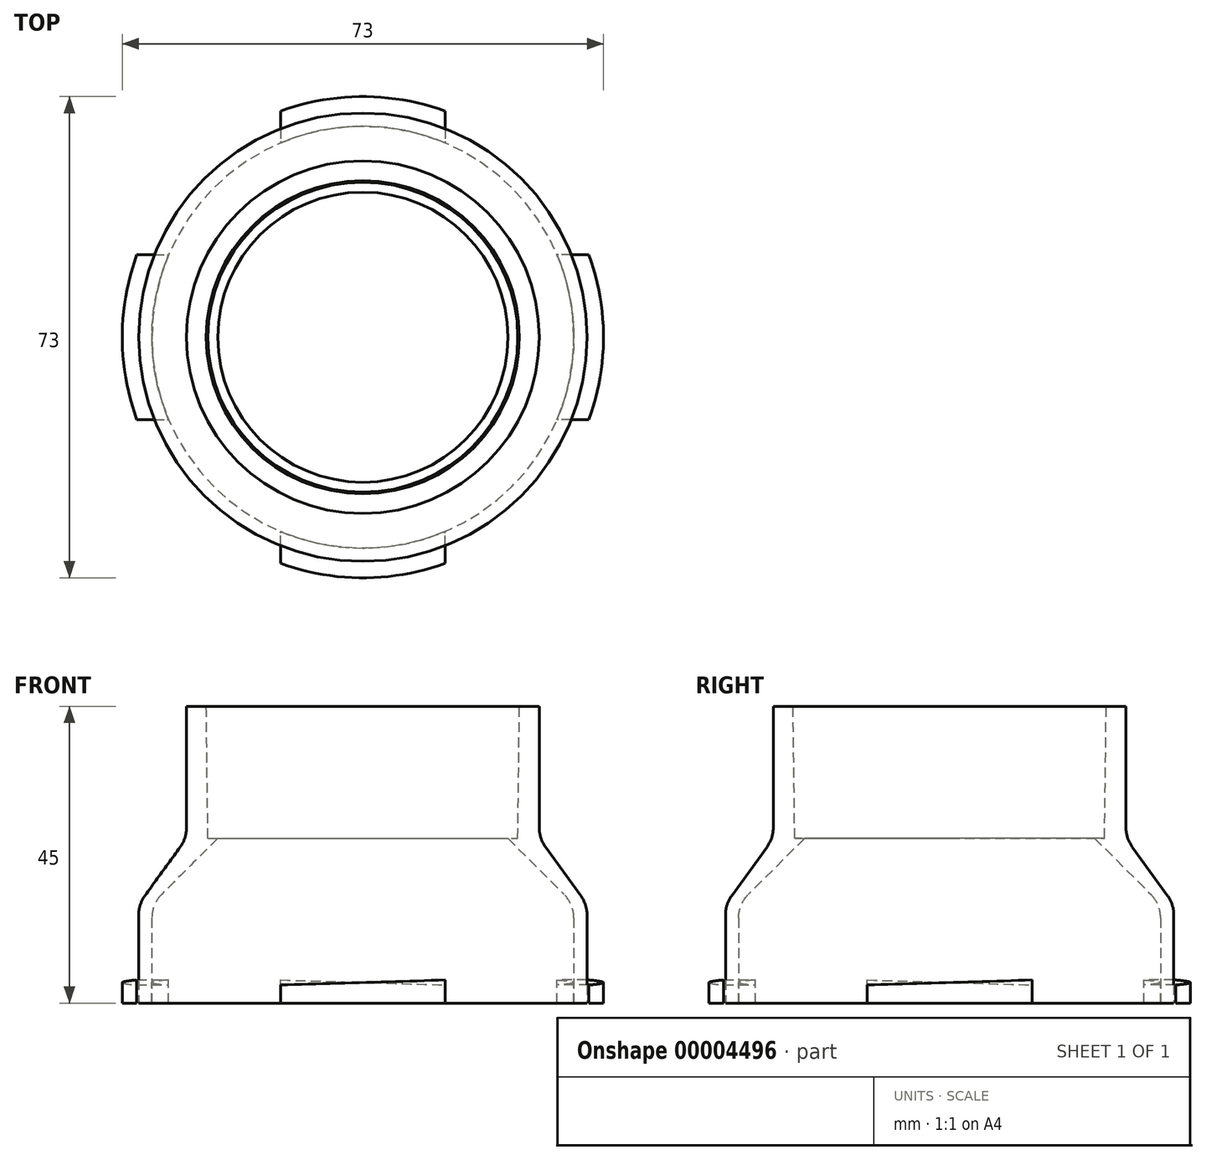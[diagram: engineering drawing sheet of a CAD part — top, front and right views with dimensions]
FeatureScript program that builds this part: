
annotation { "Feature Type Name" : "Feature", "Feature Type Description" : "" }
export const myFeature = defineFeature(function(context is Context, id is Id, definition is map)
    precondition{}
    {
        {
            var Q0;
            Q0=qCreatedBy(makeId("Front.planeOp"),FACE);
            var sketch = newSketch(context, id + "F0", { "sketchPlane" : qUnion([Q0])});
            skLineSegment(sketch, "E0", {"start": v(0, 0) * mm, "end": v(0, 61.44) * mm, "construction": true});
            skLineSegment(sketch, "E1", {"start": v(-32, 15) * mm, "end": v(-32, 0) * mm});
            skLineSegment(sketch, "E2", {"start": v(-32, 0) * mm, "end": v(-34, 0) * mm});
            skLineSegment(sketch, "E3", {"start": v(-34, 0) * mm, "end": v(-34, 15) * mm});
            skLineSegment(sketch, "E4.bottom", {"start": v(-26.75, 45) * mm, "end": v(-23.75, 45) * mm});
            skLineSegment(sketch, "E4.left", {"start": v(-26.75, 45) * mm, "end": v(-26.75, 25) * mm});
            skLineSegment(sketch, "E5", {"start": v(-26.75, 25) * mm, "end": v(-34, 15) * mm});
            skLineSegment(sketch, "E6", {"start": v(-32, 15) * mm, "end": v(-22, 25) * mm});
            skLineSegment(sketch, "E7", {"start": v(-23.75, 45) * mm, "end": v(-23.5, 25) * mm});
            skLineSegment(sketch, "E8", {"start": v(-23.5, 25) * mm, "end": v(-22, 25) * mm});
            skSolve(sketch);
        }
        {
            var Q0;
            Q0=makeQuery(id+"F0.imprint","IMPRINT",FACE,{"disambiguationData":[TD([[makeQuery(id+"F0.imprint","IMPRINT",EDGE,{"derivedFrom":sQuery(id+"F0.wireOp",EDGE,"E1")}),-1.0]])]});
            var Q1;
            Q1=sQuery(id+"F0.wireOp",EDGE,"E0");
            revolve(context, id + "F1", {"entities" : qUnion([Q0]), "axis" : qUnion([Q1]), "revolveType" : RevolveType.FULL});
        }
        {
            var Q0;
            Q0=qCreatedBy(makeId("Front.planeOp"),FACE);
            var sketch = newSketch(context, id + "F2", { "sketchPlane" : qUnion([Q0])});
            skLineSegment(sketch, "E9.top", {"start": v(12.5, 0) * mm, "end": v(0, 0) * mm});
            skLineSegment(sketch, "E9.left", {"start": v(12.5, 2.75) * mm, "end": v(12.5, 0) * mm});
            skLineSegment(sketch, "E10", {"start": v(0, -1.37) * mm, "end": v(0, 27.04) * mm, "construction": true});
            skLineSegment(sketch, "E11", {"start": v(0, 0) * mm, "end": v(-12.5, 0) * mm});
            skLineSegment(sketch, "E12", {"start": v(-12.5, 0) * mm, "end": v(-12.5, 3.5) * mm});
            skLineSegment(sketch, "E13", {"start": v(-12.5, 3.5) * mm, "end": v(12.5, 2.75) * mm});
            skSolve(sketch);
        }
        {
            var Q0;
            Q0=qSketchRegion(id+"F2",true);
            extrude(context, id + "F3", {"entities" : qUnion([Q0]), "oppositeDirection" : true, "depth" : (73 / 2) * mm});
        }
        {
            var Q0;
            Q0=qCreatedBy(makeId("Right.planeOp"),FACE);
            var sketch = newSketch(context, id + "F4", { "sketchPlane" : qUnion([Q0])});
            skLineSegment(sketch, "E14.0", {"start": v(36.5, 0) * mm, "end": v(36.5, 3.5) * mm});
            skLineSegment(sketch, "E15.0", {"start": v(34, 15) * mm, "end": v(-34, 15) * mm, "construction": true});
            skLineSegment(sketch, "E16", {"start": v(0, 0) * mm, "end": v(0, 34.86) * mm, "construction": true});
            skLineSegment(sketch, "E17.bottom", {"start": v(36.5, 3.5) * mm, "end": v(46.5, 3.5) * mm});
            skLineSegment(sketch, "E17.top", {"start": v(36.5, 0) * mm, "end": v(46.5, 0) * mm});
            skLineSegment(sketch, "E17.left", {"start": v(36.5, 3.5) * mm, "end": v(36.5, 0) * mm});
            skLineSegment(sketch, "E17.right", {"start": v(46.5, 3.5) * mm, "end": v(46.5, 0) * mm});
            skLineSegment(sketch, "E18.bottom", {"start": v(36.5, 0) * mm, "end": v(36.5, 0) * mm});
            skLineSegment(sketch, "E18.top", {"start": v(36.5, 0) * mm, "end": v(36.5, 0) * mm});
            skLineSegment(sketch, "E18.left", {"start": v(36.5, 0) * mm, "end": v(36.5, 0) * mm});
            skLineSegment(sketch, "E18.right", {"start": v(36.5, 0) * mm, "end": v(36.5, 0) * mm});
            skLineSegment(sketch, "E19.0", {"start": v(32, 0) * mm, "end": v(-32, 0) * mm, "construction": true});
            skLineSegment(sketch, "E20.bottom", {"start": v(32, 0) * mm, "end": v(0, 0) * mm});
            skLineSegment(sketch, "E20.top", {"start": v(32, 3.5) * mm, "end": v(0, 3.5) * mm});
            skLineSegment(sketch, "E20.left", {"start": v(32, 0) * mm, "end": v(32, 3.5) * mm});
            skLineSegment(sketch, "E20.right", {"start": v(0, 0) * mm, "end": v(0, 3.5) * mm});
            skSolve(sketch);
        }
        {
            var Q0;
            {Q0=qUnion([makeQuery(id+"F4.imprint","IMPRINT",FACE,{"disambiguationData":[TD([[makeQuery(id+"F4.imprint","IMPRINT",EDGE,{"derivedFrom":sQuery(id+"F4.wireOp",EDGE,"E17.bottom")}),-1.0]])]}),makeQuery(id+"F4.imprint","IMPRINT",FACE,{"disambiguationData":[TD([[makeQuery(id+"F4.imprint","IMPRINT",EDGE,{"derivedFrom":sQuery(id+"F4.wireOp",EDGE,"E20.bottom")}),-1.0]])]})]);}
            var Q1;
            Q1=sQuery(id+"F4.wireOp",EDGE,"E16");
            revolve(context, id + "F5", {"operationType" : NewBodyOperationType.REMOVE, "entities" : qUnion([Q0]), "axis" : qUnion([Q1]), "revolveType" : RevolveType.FULL, "oppositeDirection" : true});
        }
        {
            var Q0;
            Q0=makeQuery(id+"F3.opExtrude","SWEPT_BODY",BODY,{"disambiguationData":[OSD([sQuery(id+"F2.wireOp",EDGE,"E9.top"),sQuery(id+"F2.wireOp",EDGE,"E9.left"),sQuery(id+"F2.wireOp",EDGE,"E12"),sQuery(id+"F2.wireOp",EDGE,"E13")])]});
            var Q1;
            Q1=sQuery(id+"F4.wireOp",EDGE,"E16");
            circularPattern(context, id + "F6", {"entities" : qUnion([Q0]), "axis" : qUnion([Q1]), "angle" : 360 * degree, "instanceCount" : round(4), "equalSpace" : true});
        }
        {
            var Q0;
            Q0=makeQuery(id+"F1.opRevolve","SWEPT_EDGE",EDGE,{"disambiguationData":[OSD([sQuery(id+"F0.wireOp",EDGE,"E1"),sQuery(id+"F0.wireOp",EDGE,"E6")])]});
            var Q1;
            Q1=makeQuery(id+"F1.opRevolve","SWEPT_EDGE",EDGE,{"disambiguationData":[OSD([sQuery(id+"F0.wireOp",EDGE,"E4.left"),sQuery(id+"F0.wireOp",EDGE,"E5")])]});
            var Q2;
            Q2=makeQuery(id+"F1.opRevolve","SWEPT_EDGE",EDGE,{"disambiguationData":[OSD([sQuery(id+"F0.wireOp",EDGE,"E3"),sQuery(id+"F0.wireOp",EDGE,"E5")])]});
            fillet(context, id + "F7", {"entities" : qUnion([Q0, Q1, Q2]), "radius" : 5 * mm, "tangentPropagation" : true, "allowEdgeOverflow" : false});
        }
    });
